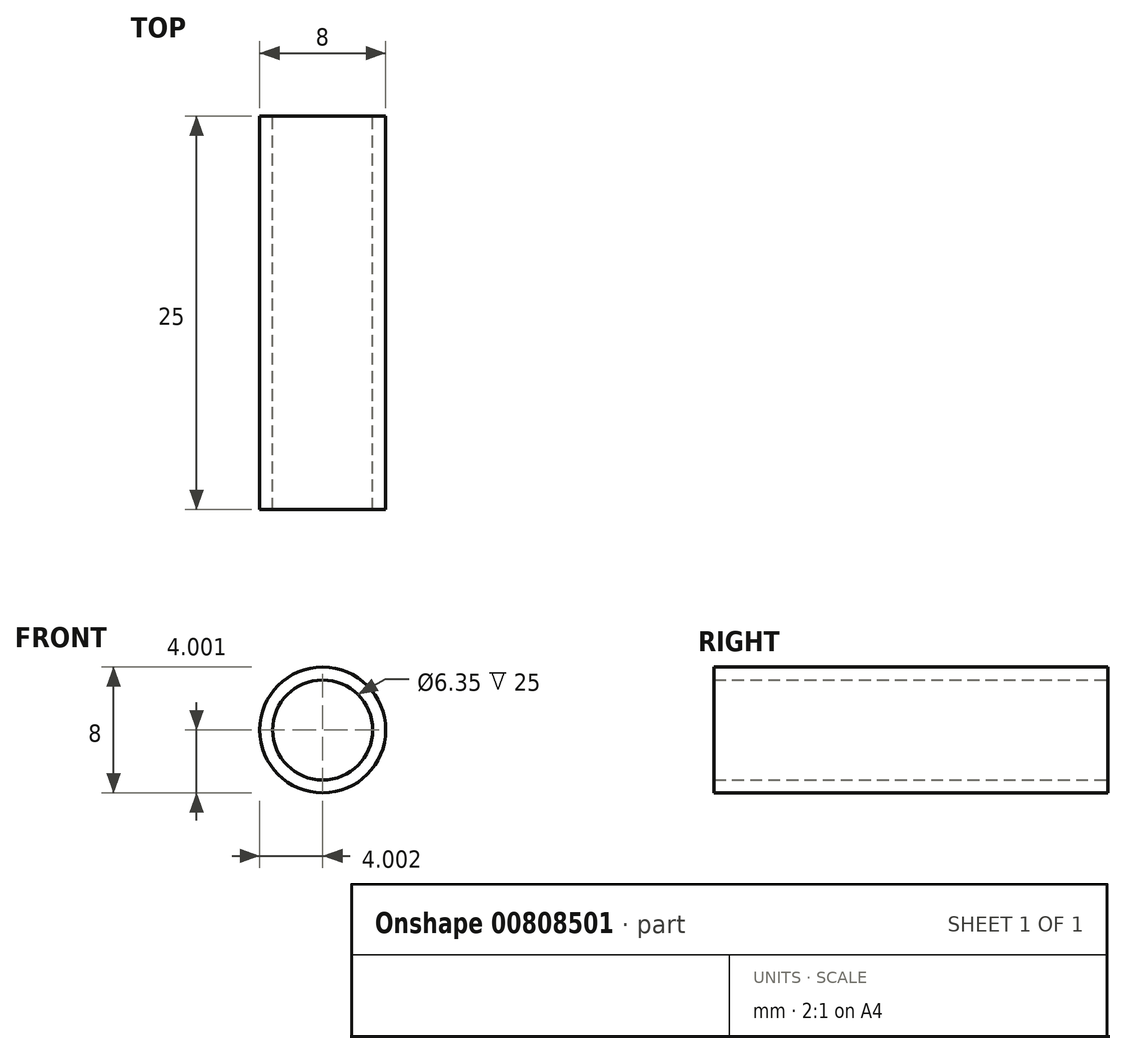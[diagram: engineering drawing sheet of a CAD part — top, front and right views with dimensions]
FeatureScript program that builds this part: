
annotation { "Feature Type Name" : "Feature", "Feature Type Description" : "" }
export const myFeature = defineFeature(function(context is Context, id is Id, definition is map)
    precondition{}
    {
        {
            var Q0;
            Q0=qCreatedBy(makeId("Front.planeOp"),FACE);
            var sketch = newSketch(context, id + "F0", { "sketchPlane" : qUnion([Q0])});
            skCircle(sketch, "E0", {"center": v(-44.13, -33.44) * mm, "radius": 3.18 * mm});
            skCircle(sketch, "E1", {"center": v(-44.13, -33.44) * mm, "radius": 4 * mm});
            skSolve(sketch);
        }
        {
            var Q0;
            Q0=makeQuery(id+"F0.imprint","IMPRINT",FACE,{"disambiguationData":[TD([[makeQuery(id+"F0.imprint","IMPRINT",EDGE,{"derivedFrom":sQuery(id+"F0.wireOp",EDGE,"E0")}),-1.0]])]});
            extrude(context, id + "F1", {"entities" : qUnion([Q0]), "depth" : 25 * mm, "offsetDistance" : 25 * mm});
        }
    });
